# Revit family: agtatec_Record_SldngDrset_E-TSA-Telescopic_Standalone
name_source: partatom
category: Doors
revit_build: Autodesk Revit Architecture 2015 (Build: 20140606_1530(x64)
units: mm (PartAtom-declared; Revit-internal decimal feet)

## types (12) — shared parameters
AccessoryOptions = Contact manufacturer
AcousticRating = None
AlternativeDoorsetGlazing = Part of glazing spec
AntiFingerTrapRequirement = Yes
Assembly Code = B2030110
BIMObjectName = agtatec_Record_SlidingDoorset_E-TSA-Telescopic_Standalone
Cladding profile = Yes
ClearHeightOfPassage = 2187 mm  [stored 7.1752 ft]
ClearanceZones = No
Colour = Customer specific
Configuration = 1 or 2
Construction Type = Automatic Sliding Door
Description = Automatic Sliding Door
Distance to Wall = 57 mm  [stored 0.187008 ft]
Door Opening 2 = 600 mm
DoorIncluded = Yes
DoorSeal = yes
DoorsetFasteners = Screws
DoorsetOperation = Automatic
Drive Depth = 259 mm  [stored 0.849738 ft]
Drive Depth 2 = 37 mm  [stored 0.121391 ft]
DriveUnit = agtatec_Record_Sliding Door, Sheet Metal (Painted Steel)
DurationUnit = year
ElectronicLock = Yes
Finish = Powder coated, Anodized, customer specific
FireExit = No
FireRating = None
FloorGuide = agtatec_Record_Sliding Door, Stainless Steel
FrameMaterial = Aluminium
FrameProfile = Aluminium
FrameSeal = Yes
Function = Exterior
GlassLayers = 2
GlassThickness1 = 6 mm (default)
GlassThickness2 = 6 mm (default)
GlassType = Part of glazing spec
GlazingAreaFraction = Depends on size. Can be calculated
HandicapAccessible = Yes
HasDrive = Yes
IfcExportAs = IfcDoorStyle
IfcExportType = Door
Inner Panel Width 1 = 632 mm
Inner Panel Width 2 = 620 mm
Interlancing Profile Height = 2195 mm  [stored 7.20144 ft]
IsExternal = Yes
LeafColourOptions = All RAL, customer specific
ManufacturerName = Record
ManufacturerURL = www.agta-record.com
Material = Aluminium
Model = record Telescopic Linear Slider
ModelReference = Depends on the configuration
NBSDescription = Sliding Doorset
NBSReference = 25-50-20/175
Name = SldngDrset_E-TSA-Telescopic_Standalone_Record
OpeningWidth = 1200 mm
Outer Panel Width Left = 673 mm
Outer Panel Width Right = 673 mm
PanelFill = agtatec_Record_Sliding Door, Laminated Safety Glass (Clear)
PanelFrames = agtatec_Record_Sliding Door, Aluminium
PanelHeight = 2200 mm
Passage Mounting Left = No
Passage Mounting Right = No
PassageMountingProfile(OnlyApplicableForTypesWithTwoSidePanels) = No
ProductInformation = www.agta-record.com
ReferenceStandard = EN16005, EN16361, DIN 18650, etc.
ReplacementCost = Depends on the configuration and door type
SecurityRating = None
SelfClosing = Yes
ServiceLifeDuration = 10-15 years
Shape = Rectangular
SidePanelWidthLeft = 700 mm  [stored 2.29659 ft]
SidePanelWidthRight = 700 mm  [stored 2.29659 ft]
SmokeStop = No
SupportLength = 1900 mm  [stored 6.2336 ft]
ThresholdRequired = Yes
ThresholdStripping = No additional required, part of the doorset
URL = www.agta-record.com
Uniclass2 = Ss_25_30_20_77
Version = Version 1.0
WallMountingProfile = Yes
WarrantyDescription = Depends on country
WarrantyDurationLabour = Depends on country
WarrantyDurationParts = Depends on country
WarrantyDurationUnit = Depends on country
WarrantyGuarantorLabour = Local door manufacturer
WarrantyGuarantorParts = Local door manufacturer
Weight = Depends on configuration and size
WithDriveCladding = Yes
WithinStandardSizes = Yes
WithoutDriveCladding(OnlyApplicableForTypesWithoutSidePanels) = No
zero-valued in all types: Cost, Door Opening 1, DoorOpening, DriveUnitExtraWidthLeft, DriveUnitExtraWidthRight, Extra Left, Extra Right, Extra Width Total, ExtraWidthLeft, ExtraWidthRight, NominalLength, ThermalTransmittance

## per-type parameters (varying)
- E-TSA-L 150 mm drive unit height - left - with side panel: CenterOfDoor=1650 mm  [stored 5.41339 ft]; Cladding void=35 mm  [stored 0.114829 ft]; ClearanceZoneLeft=966 mm; ClearanceZoneRight=1005 mm  [stored 3.29724 ft]; DriveUnitHeight=150 mm; Height=2337 mm  [stored 7.66732 ft]; InterlancingProfileLeft=No; InterlancingProfileRight=No; Left=Yes; Left Panel=Yes; Left Profile=Yes; NominalHeight=2337 mm  [stored 7.66732 ft]; NominalWidth=1955 mm  [stored 6.41404 ft]; Right=No; Right Panel=No; Right Profile=No; Rough Height=2343 mm  [stored 7.68701 ft]; Rough Width=1961 mm  [stored 6.43373 ft]; Support Length Left=1300 mm  [stored 4.26509 ft]; Support Length Right=600 mm; TotalHeight=2337 mm  [stored 7.66732 ft]; TotalWidth=1955 mm  [stored 6.41404 ft]; Wall Mounting Left=Yes; Wall Mounting Right=No; Wall Opening Width=1900 mm  [stored 6.2336 ft]; Width=1955 mm  [stored 6.41404 ft]; Without side panels=No
- E-TSA-R 150 mm drive unit height - right - without side panel: CenterOfDoor=950 mm  [stored 3.1168 ft]; Cladding void=3 mm  [stored 0.00984252 ft]; ClearanceZoneLeft=1005 mm  [stored 3.29724 ft]; ClearanceZoneRight=950 mm  [stored 3.1168 ft]; DriveUnitHeight=150 mm; Height=2337 mm  [stored 7.66732 ft]; InterlancingProfileLeft=No; InterlancingProfileRight=Yes; Left=No; Left Panel=No; Left Profile=No; NominalHeight=2337 mm  [stored 7.66732 ft]; NominalWidth=1299 mm  [stored 4.26181 ft]; Right=Yes; Right Panel=No; Right Profile=No; Rough Height=2343 mm  [stored 7.68701 ft]; Rough Width=1305 mm  [stored 4.2815 ft]; Support Length Left=600 mm; Support Length Right=1300 mm  [stored 4.26509 ft]; TotalHeight=2337 mm  [stored 7.66732 ft]; TotalWidth=1299 mm  [stored 4.26181 ft]; Wall Mounting Left=No; Wall Mounting Right=No; Wall Opening Width=1200 mm; Width=1299 mm  [stored 4.26181 ft]; Without side panels=Yes
- E-TSA-R 150 mm drive unit height - right - with side panel: CenterOfDoor=950 mm  [stored 3.1168 ft]; Cladding void=35 mm  [stored 0.114829 ft]; ClearanceZoneLeft=1005 mm  [stored 3.29724 ft]; ClearanceZoneRight=966 mm; DriveUnitHeight=150 mm; Height=2337 mm  [stored 7.66732 ft]; InterlancingProfileLeft=No; InterlancingProfileRight=No; Left=No; Left Panel=No; Left Profile=No; NominalHeight=2337 mm  [stored 7.66732 ft]; NominalWidth=1955 mm  [stored 6.41404 ft]; Right=Yes; Right Panel=Yes; Right Profile=Yes; Rough Height=2343 mm  [stored 7.68701 ft]; Rough Width=1961 mm  [stored 6.43373 ft]; Support Length Left=600 mm; Support Length Right=1300 mm  [stored 4.26509 ft]; TotalHeight=2337 mm  [stored 7.66732 ft]; TotalWidth=1955 mm  [stored 6.41404 ft]; Wall Mounting Left=No; Wall Mounting Right=Yes; Wall Opening Width=1900 mm  [stored 6.2336 ft]; Width=1955 mm  [stored 6.41404 ft]; Without side panels=No
- E-TSA-L 150 mm drive unit height - left - without side panel: CenterOfDoor=1650 mm  [stored 5.41339 ft]; Cladding void=3 mm  [stored 0.00984252 ft]; ClearanceZoneLeft=950 mm  [stored 3.1168 ft]; ClearanceZoneRight=1005 mm  [stored 3.29724 ft]; DriveUnitHeight=150 mm; Height=2337 mm  [stored 7.66732 ft]; InterlancingProfileLeft=Yes; InterlancingProfileRight=No; Left=Yes; Left Panel=No; Left Profile=No; NominalHeight=2337 mm  [stored 7.66732 ft]; NominalWidth=1299 mm  [stored 4.26181 ft]; Right=No; Right Panel=No; Right Profile=No; Rough Height=2343 mm  [stored 7.68701 ft]; Rough Width=1305 mm  [stored 4.2815 ft]; Support Length Left=1300 mm  [stored 4.26509 ft]; Support Length Right=600 mm; TotalHeight=2337 mm  [stored 7.66732 ft]; TotalWidth=1299 mm  [stored 4.26181 ft]; Wall Mounting Left=No; Wall Mounting Right=No; Wall Opening Width=1200 mm; Width=1299 mm  [stored 4.26181 ft]; Without side panels=Yes
- E-TSA-L 200 mm drive unit height - left - with side panel: CenterOfDoor=1650 mm  [stored 5.41339 ft]; Cladding void=35 mm  [stored 0.114829 ft]; ClearanceZoneLeft=966 mm; ClearanceZoneRight=1005 mm  [stored 3.29724 ft]; DriveUnitHeight=200 mm  [stored 0.656168 ft]; Height=2387 mm  [stored 7.83136 ft]; InterlancingProfileLeft=No; InterlancingProfileRight=No; Left=Yes; Left Panel=Yes; Left Profile=Yes; NominalHeight=2387 mm  [stored 7.83136 ft]; NominalWidth=1955 mm  [stored 6.41404 ft]; Right=No; Right Panel=No; Right Profile=No; Rough Height=2393 mm  [stored 7.85105 ft]; Rough Width=1961 mm  [stored 6.43373 ft]; Support Length Left=1300 mm  [stored 4.26509 ft]; Support Length Right=600 mm; TotalHeight=2387 mm  [stored 7.83136 ft]; TotalWidth=1955 mm  [stored 6.41404 ft]; Wall Mounting Left=Yes; Wall Mounting Right=No; Wall Opening Width=1900 mm  [stored 6.2336 ft]; Width=1955 mm  [stored 6.41404 ft]; Without side panels=No
- E-TSA-L 200 mm drive unit height - left - without side panel: CenterOfDoor=1650 mm  [stored 5.41339 ft]; Cladding void=3 mm  [stored 0.00984252 ft]; ClearanceZoneLeft=950 mm  [stored 3.1168 ft]; ClearanceZoneRight=1005 mm  [stored 3.29724 ft]; DriveUnitHeight=200 mm  [stored 0.656168 ft]; Height=2387 mm  [stored 7.83136 ft]; InterlancingProfileLeft=Yes; InterlancingProfileRight=No; Left=Yes; Left Panel=No; Left Profile=No; NominalHeight=2387 mm  [stored 7.83136 ft]; NominalWidth=1299 mm  [stored 4.26181 ft]; Right=No; Right Panel=No; Right Profile=No; Rough Height=2393 mm  [stored 7.85105 ft]; Rough Width=1305 mm  [stored 4.2815 ft]; Support Length Left=1300 mm  [stored 4.26509 ft]; Support Length Right=600 mm; TotalHeight=2387 mm  [stored 7.83136 ft]; TotalWidth=1299 mm  [stored 4.26181 ft]; Wall Mounting Left=No; Wall Mounting Right=No; Wall Opening Width=1200 mm; Width=1299 mm  [stored 4.26181 ft]; Without side panels=Yes
- E-TSA-R 200 mm drive unit height - right - with side panel: CenterOfDoor=950 mm  [stored 3.1168 ft]; Cladding void=35 mm  [stored 0.114829 ft]; ClearanceZoneLeft=1005 mm  [stored 3.29724 ft]; ClearanceZoneRight=966 mm; DriveUnitHeight=200 mm  [stored 0.656168 ft]; Height=2387 mm  [stored 7.83136 ft]; InterlancingProfileLeft=No; InterlancingProfileRight=No; Left=No; Left Panel=No; Left Profile=No; NominalHeight=2387 mm  [stored 7.83136 ft]; NominalWidth=1955 mm  [stored 6.41404 ft]; Right=Yes; Right Panel=Yes; Right Profile=Yes; Rough Height=2393 mm  [stored 7.85105 ft]; Rough Width=1961 mm  [stored 6.43373 ft]; Support Length Left=600 mm; Support Length Right=1300 mm  [stored 4.26509 ft]; TotalHeight=2387 mm  [stored 7.83136 ft]; TotalWidth=1955 mm  [stored 6.41404 ft]; Wall Mounting Left=No; Wall Mounting Right=Yes; Wall Opening Width=1900 mm  [stored 6.2336 ft]; Width=1955 mm  [stored 6.41404 ft]; Without side panels=No
- E-TSA-R 200 mm drive unit height - right - without side panel: CenterOfDoor=950 mm  [stored 3.1168 ft]; Cladding void=3 mm  [stored 0.00984252 ft]; ClearanceZoneLeft=1005 mm  [stored 3.29724 ft]; ClearanceZoneRight=950 mm  [stored 3.1168 ft]; DriveUnitHeight=200 mm  [stored 0.656168 ft]; Height=2387 mm  [stored 7.83136 ft]; InterlancingProfileLeft=No; InterlancingProfileRight=Yes; Left=No; Left Panel=No; Left Profile=No; NominalHeight=2387 mm  [stored 7.83136 ft]; NominalWidth=1299 mm  [stored 4.26181 ft]; Right=Yes; Right Panel=No; Right Profile=No; Rough Height=2393 mm  [stored 7.85105 ft]; Rough Width=1305 mm  [stored 4.2815 ft]; Support Length Left=600 mm; Support Length Right=1300 mm  [stored 4.26509 ft]; TotalHeight=2387 mm  [stored 7.83136 ft]; TotalWidth=1299 mm  [stored 4.26181 ft]; Wall Mounting Left=No; Wall Mounting Right=No; Wall Opening Width=1200 mm; Width=1299 mm  [stored 4.26181 ft]; Without side panels=Yes
- E-TSA-L 108 mm drive unit height - left - with side panel: CenterOfDoor=1650 mm  [stored 5.41339 ft]; Cladding void=35 mm  [stored 0.114829 ft]; ClearanceZoneLeft=966 mm; ClearanceZoneRight=1005 mm  [stored 3.29724 ft]; DriveUnitHeight=108 mm  [stored 0.354331 ft]; Height=2295 mm; InterlancingProfileLeft=No; InterlancingProfileRight=No; Left=Yes; Left Panel=Yes; Left Profile=Yes; NominalHeight=2295 mm; NominalWidth=1955 mm  [stored 6.41404 ft]; Right=No; Right Panel=No; Right Profile=No; Rough Height=2301 mm; Rough Width=1961 mm  [stored 6.43373 ft]; Support Length Left=1300 mm  [stored 4.26509 ft]; Support Length Right=600 mm; TotalHeight=2295 mm; TotalWidth=1955 mm  [stored 6.41404 ft]; Wall Mounting Left=Yes; Wall Mounting Right=No; Wall Opening Width=1900 mm  [stored 6.2336 ft]; Width=1955 mm  [stored 6.41404 ft]; Without side panels=No
- E-TSA-L 108 mm drive unit height - left - without side panel: CenterOfDoor=1650 mm  [stored 5.41339 ft]; Cladding void=3 mm  [stored 0.00984252 ft]; ClearanceZoneLeft=950 mm  [stored 3.1168 ft]; ClearanceZoneRight=1005 mm  [stored 3.29724 ft]; DriveUnitHeight=108 mm  [stored 0.354331 ft]; Height=2295 mm; InterlancingProfileLeft=Yes; InterlancingProfileRight=No; Left=Yes; Left Panel=No; Left Profile=No; NominalHeight=2295 mm; NominalWidth=1299 mm  [stored 4.26181 ft]; Right=No; Right Panel=No; Right Profile=No; Rough Height=2301 mm; Rough Width=1305 mm  [stored 4.2815 ft]; Support Length Left=1300 mm  [stored 4.26509 ft]; Support Length Right=600 mm; TotalHeight=2295 mm; TotalWidth=1299 mm  [stored 4.26181 ft]; Wall Mounting Left=No; Wall Mounting Right=No; Wall Opening Width=1200 mm; Width=1299 mm  [stored 4.26181 ft]; Without side panels=Yes
- E-TSA-R 108 mm drive unit height - right - with side panel: CenterOfDoor=950 mm  [stored 3.1168 ft]; Cladding void=35 mm  [stored 0.114829 ft]; ClearanceZoneLeft=1005 mm  [stored 3.29724 ft]; ClearanceZoneRight=966 mm; DriveUnitHeight=108 mm  [stored 0.354331 ft]; Height=2295 mm; InterlancingProfileLeft=No; InterlancingProfileRight=No; Left=No; Left Panel=No; Left Profile=No; NominalHeight=2295 mm; NominalWidth=1955 mm  [stored 6.41404 ft]; Right=Yes; Right Panel=Yes; Right Profile=Yes; Rough Height=2301 mm; Rough Width=1961 mm  [stored 6.43373 ft]; Support Length Left=600 mm; Support Length Right=1300 mm  [stored 4.26509 ft]; TotalHeight=2295 mm; TotalWidth=1955 mm  [stored 6.41404 ft]; Wall Mounting Left=No; Wall Mounting Right=Yes; Wall Opening Width=1900 mm  [stored 6.2336 ft]; Width=1955 mm  [stored 6.41404 ft]; Without side panels=No
- E-TSA-R 108 mm drive unit height - right - without side panel: CenterOfDoor=950 mm  [stored 3.1168 ft]; Cladding void=3 mm  [stored 0.00984252 ft]; ClearanceZoneLeft=1005 mm  [stored 3.29724 ft]; ClearanceZoneRight=950 mm  [stored 3.1168 ft]; DriveUnitHeight=108 mm  [stored 0.354331 ft]; Height=2295 mm; InterlancingProfileLeft=No; InterlancingProfileRight=Yes; Left=No; Left Panel=No; Left Profile=No; NominalHeight=2295 mm; NominalWidth=1299 mm  [stored 4.26181 ft]; Right=Yes; Right Panel=No; Right Profile=No; Rough Height=2301 mm; Rough Width=1305 mm  [stored 4.2815 ft]; Support Length Left=600 mm; Support Length Right=1300 mm  [stored 4.26509 ft]; TotalHeight=2295 mm; TotalWidth=1299 mm  [stored 4.26181 ft]; Wall Mounting Left=No; Wall Mounting Right=No; Wall Opening Width=1200 mm; Width=1299 mm  [stored 4.26181 ft]; Without side panels=Yes

note: [stored X ft] marks values corroborated as IEEE doubles in the binary element streams (Revit-internal decimal feet)

## geometry (parser evidence)
native form markers: Sweep x14
no freeform markers — native parametric forms only
